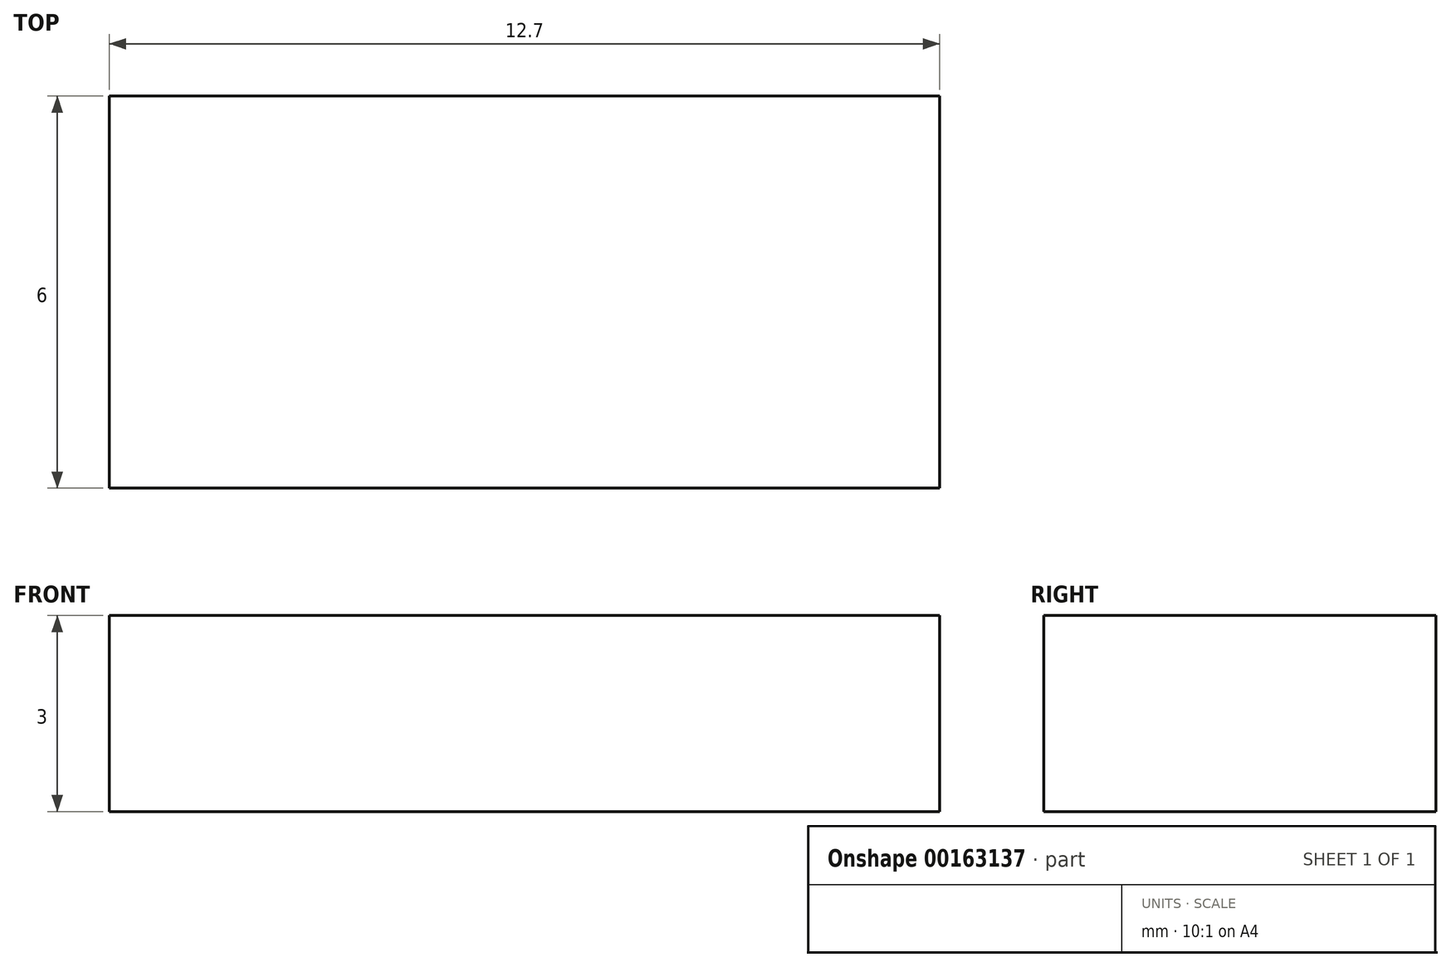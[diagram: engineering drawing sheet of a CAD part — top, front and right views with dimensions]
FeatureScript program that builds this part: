
annotation { "Feature Type Name" : "Feature", "Feature Type Description" : "" }
export const myFeature = defineFeature(function(context is Context, id is Id, definition is map)
    precondition{}
    {
        {
            var Q0;
            Q0=qCreatedBy(makeId("Front.planeOp"),FACE);
            var sketch = newSketch(context, id + "F0", { "sketchPlane" : qUnion([Q0])});
            skLineSegment(sketch, "E0.bottom", {"start": v(-6.35, 1.5) * mm, "end": v(6.35, 1.5) * mm});
            skLineSegment(sketch, "E0.top", {"start": v(-6.35, -1.5) * mm, "end": v(6.35, -1.5) * mm});
            skLineSegment(sketch, "E0.left", {"start": v(-6.35, 1.5) * mm, "end": v(-6.35, -1.5) * mm});
            skLineSegment(sketch, "E0.right", {"start": v(6.35, 1.5) * mm, "end": v(6.35, -1.5) * mm});
            skPoint(sketch, "E0.middle", {"position": v(0, 0) * mm});
            skSolve(sketch);
        }
        {
            var Q0;
            Q0 = qSketchRegion(id + "F0", true);
            extrude(context, id + "F1", {"entities" : qUnion([Q0]), "depth" : 6 * mm});
        }
    });
